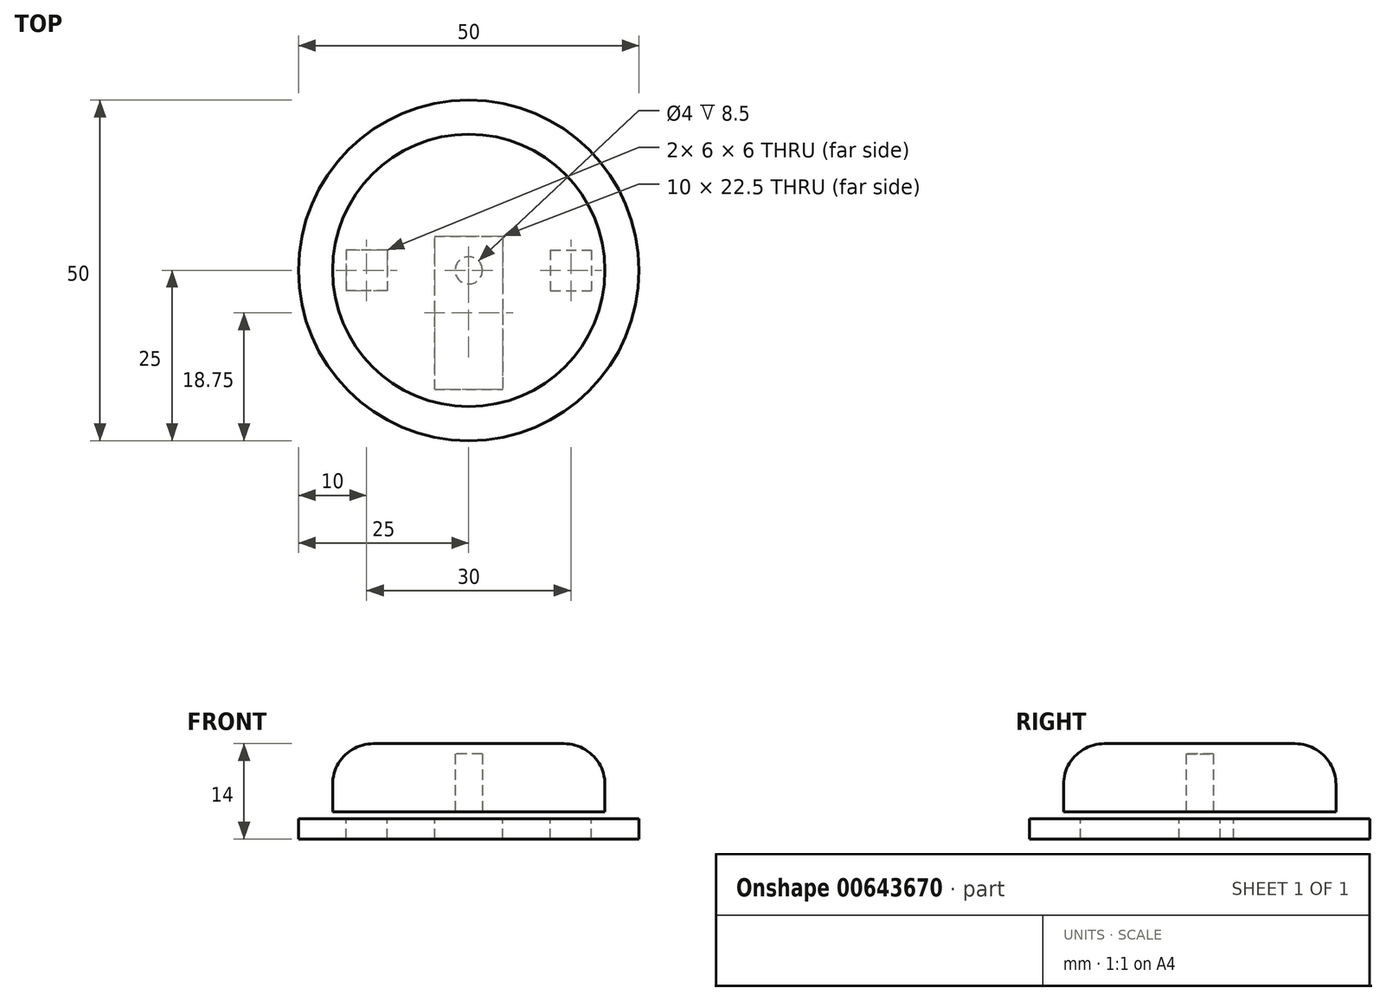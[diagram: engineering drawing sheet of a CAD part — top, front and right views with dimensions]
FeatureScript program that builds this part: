
annotation { "Feature Type Name" : "Feature", "Feature Type Description" : "" }
export const myFeature = defineFeature(function(context is Context, id is Id, definition is map)
    precondition{}
    {
        {
            var Q0;
            Q0=qCreatedBy(makeId("Top.planeOp"),FACE);
            var sketch = newSketch(context, id + "F0", { "sketchPlane" : qUnion([Q0])});
            skCircle(sketch, "E0", {"center": v(0, 0) * mm, "radius": 25 * mm});
            skSolve(sketch);
        }
        {
            var Q0;
            Q0=makeQuery(id+"F0.imprint","IMPRINT",FACE,{"disambiguationData":[TD([[makeQuery(id+"F0.imprint","IMPRINT",EDGE,{"derivedFrom":sQuery(id+"F0.wireOp",EDGE,"E0")}),1.0]])]});
            extrude(context, id + "F1", {"entities" : qUnion([Q0]), "depth" : 3 * mm, "offsetDistance" : 25 * mm});
        }
        {
            var Q0;
            Q0=makeQuery(id+"F1.opExtrude","CAP_FACE",FACE,{"disambiguationData":[OSD([sQuery(id+"F0.wireOp",EDGE,"E0")])],"isStart":false});
            var sketch = newSketch(context, id + "F2", { "sketchPlane" : qUnion([Q0])});
            skLineSegment(sketch, "E1.top", {"start": v(-5, -17.5) * mm, "end": v(5, -17.5) * mm});
            skLineSegment(sketch, "E1.left", {"start": v(-5, 0) * mm, "end": v(-5, -17.5) * mm});
            skLineSegment(sketch, "E1.right", {"start": v(5, 0) * mm, "end": v(5, -17.5) * mm});
            skLineSegment(sketch, "E2.top", {"start": v(-5, 5) * mm, "end": v(5, 5) * mm});
            skLineSegment(sketch, "E2.left", {"start": v(-5, 0) * mm, "end": v(-5, 5) * mm});
            skLineSegment(sketch, "E2.right", {"start": v(5, 0) * mm, "end": v(5, 5) * mm});
            skSolve(sketch);
        }
        {
            var Q0;
            Q0=makeQuery(id+"F2.imprint","IMPRINT",FACE,{"disambiguationData":[TD([[makeQuery(id+"F2.imprint","IMPRINT",EDGE,{"derivedFrom":sQuery(id+"F2.wireOp",EDGE,"E1.top")}),1.0]])]});
            extrude(context, id + "F3", {"entities" : qUnion([Q0]), "operationType" : NewBodyOperationType.REMOVE, "oppositeDirection" : true, "depth" : 25 * mm, "offsetDistance" : 25 * mm});
        }
        {
            var Q0;
            Q0=qCreatedBy(makeId("Top.planeOp"),FACE);
            cPlane(context, id + "F4", {"entities" : qUnion([Q0]), "cplaneType" : CPlaneType.OFFSET, "offset" : 4 * mm, "width" : 150 * mm, "height" : 150 * mm});
        }
        {
            var Q0;
            Q0=qCreatedBy(id+"F4.planeOp",FACE);
            var sketch = newSketch(context, id + "F5", { "sketchPlane" : qUnion([Q0])});
            skCircle(sketch, "E3", {"center": v(0, 0) * mm, "radius": 20 * mm});
            skCircle(sketch, "E4", {"center": v(0, 0) * mm, "radius": 2 * mm});
            skSolve(sketch);
        }
        {
            var Q0;
            Q0=makeQuery(id+"F5.imprint","IMPRINT",FACE,{"disambiguationData":[TD([[makeQuery(id+"F5.imprint","IMPRINT",EDGE,{"derivedFrom":sQuery(id+"F5.wireOp",EDGE,"E3")}),1.0]])]});
            extrude(context, id + "F6", {"entities" : qUnion([Q0]), "depth" : 10 * mm, "offsetDistance" : 25 * mm});
        }
        {
            var Q0;
            Q0=makeQuery(id+"F6.opExtrude","CAP_FACE",FACE,{"disambiguationData":[OSD([sQuery(id+"F5.wireOp",EDGE,"E3"),sQuery(id+"F5.wireOp",EDGE,"E4")])],"isStart":false});
            var sketch = newSketch(context, id + "F7", { "sketchPlane" : qUnion([Q0])});
            skCircle(sketch, "E5", {"center": v(0, 0) * mm, "radius": 2 * mm});
            skSolve(sketch);
        }
        {
            var Q0;
            Q0=makeQuery(id+"F7.imprint","IMPRINT",FACE,{"disambiguationData":[TD([[makeQuery(id+"F7.imprint","IMPRINT",EDGE,{"derivedFrom":sQuery(id+"F7.wireOp",EDGE,"E5")}),1.0]])]});
            extrude(context, id + "F8", {"entities" : qUnion([Q0]), "operationType" : NewBodyOperationType.ADD, "oppositeDirection" : true, "depth" : 1.5 * mm, "offsetDistance" : 25 * mm});
        }
        {
            var Q0;
            Q0=makeQuery(id+"F6.opExtrude","CAP_EDGE",EDGE,{"disambiguationData":[OSD([sQuery(id+"F5.wireOp",EDGE,"E3")])],"isStart":false});
            fillet(context, id + "F9", {"entities" : qUnion([Q0]), "radius" : 6 * mm, "tangentPropagation" : true, "allowEdgeOverflow" : false});
        }
        {
            var Q0;
            Q0=makeQuery(id+"F1.opExtrude","CAP_FACE",FACE,{"disambiguationData":[OSD([sQuery(id+"F0.wireOp",EDGE,"E0")])],"isStart":false});
            var sketch = newSketch(context, id + "F10", { "sketchPlane" : qUnion([Q0])});
            skLineSegment(sketch, "E6.bottom", {"start": v(-12, 3) * mm, "end": v(-18, 3) * mm});
            skLineSegment(sketch, "E6.top", {"start": v(-12, -3) * mm, "end": v(-18, -3) * mm});
            skLineSegment(sketch, "E6.left", {"start": v(-12, 3) * mm, "end": v(-12, -3) * mm});
            skLineSegment(sketch, "E6.right", {"start": v(-18, 3) * mm, "end": v(-18, -3) * mm});
            skPoint(sketch, "E6.middle", {"position": v(-15, 0) * mm});
            skLineSegment(sketch, "E7.MirrorCS", {"start": v(12, 3) * mm, "end": v(12, -3) * mm});
            skLineSegment(sketch, "E8.MirrorCS", {"start": v(12, -3) * mm, "end": v(18, -3) * mm});
            skLineSegment(sketch, "E9.MirrorCS", {"start": v(12, 3) * mm, "end": v(18, 3) * mm});
            skPoint(sketch, "E10.MirrorP", {"position": v(15, 0) * mm});
            skLineSegment(sketch, "E11.MirrorCS", {"start": v(18, 3) * mm, "end": v(18, -3) * mm});
            skSolve(sketch);
        }
        {
            var Q0;
            Q0=makeQuery(id+"F10.imprint","IMPRINT",FACE,{"disambiguationData":[TD([[makeQuery(id+"F10.imprint","IMPRINT",EDGE,{"derivedFrom":sQuery(id+"F10.wireOp",EDGE,"E6.bottom")}),1.0]])]});
            var Q1;
            Q1=makeQuery(id+"F10.imprint","IMPRINT",FACE,{"disambiguationData":[TD([[makeQuery(id+"F10.imprint","IMPRINT",EDGE,{"derivedFrom":sQuery(id+"F10.wireOp",EDGE,"E7.MirrorCS")}),1.0]])]});
            extrude(context, id + "F11", {"entities" : qUnion([Q0, Q1]), "operationType" : NewBodyOperationType.REMOVE, "oppositeDirection" : true, "depth" : 25 * mm, "offsetDistance" : 25 * mm});
        }
    });
